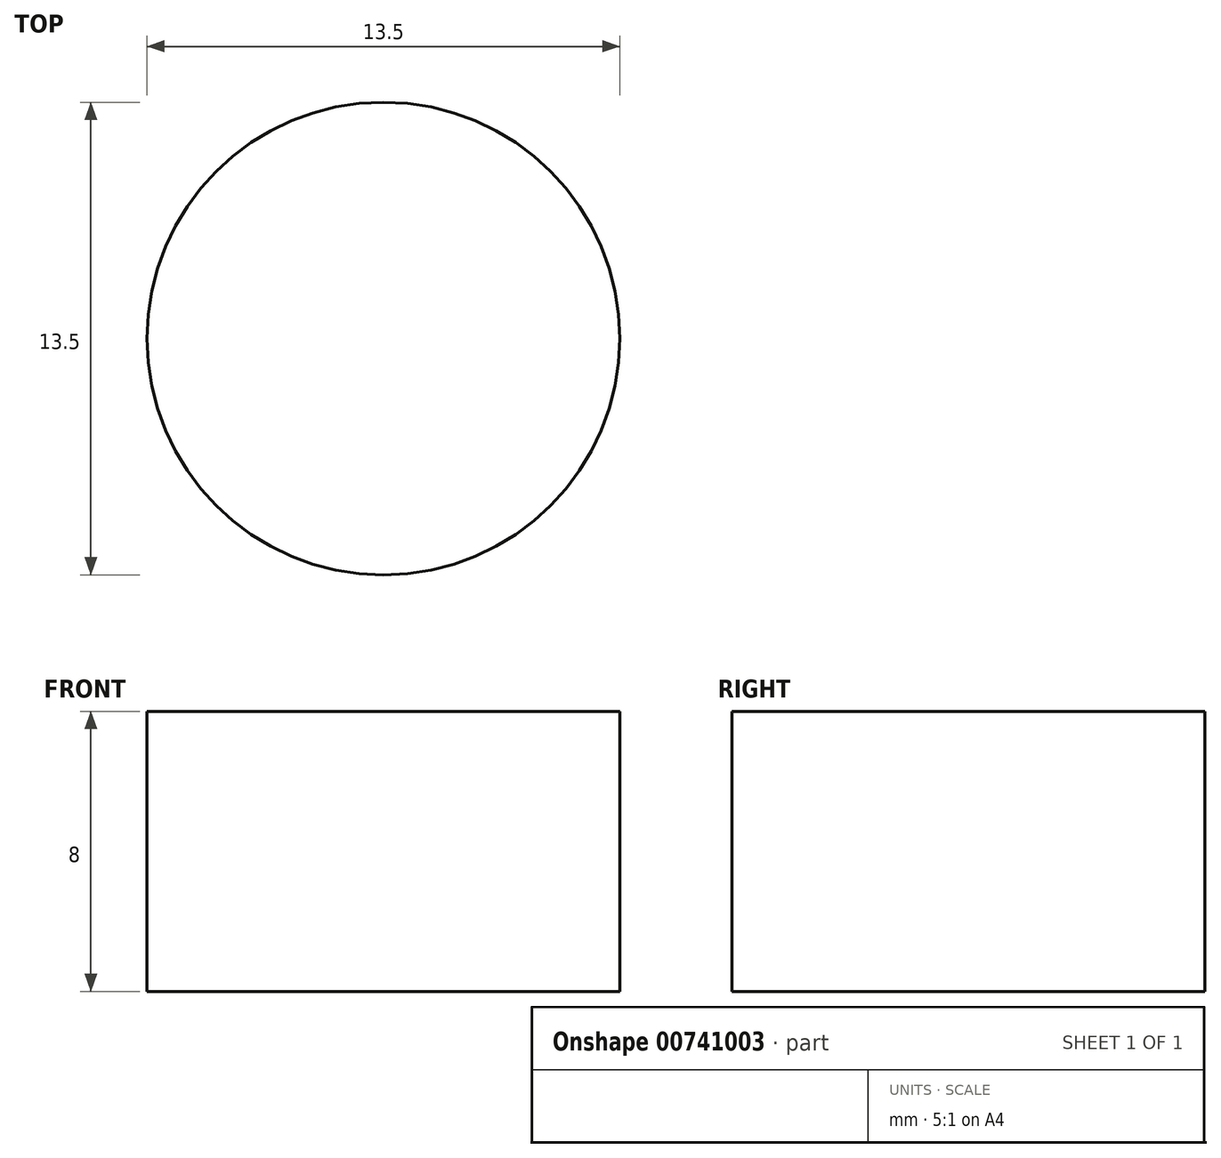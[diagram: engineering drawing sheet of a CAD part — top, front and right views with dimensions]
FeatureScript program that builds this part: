
annotation { "Feature Type Name" : "Feature", "Feature Type Description" : "" }
export const myFeature = defineFeature(function(context is Context, id is Id, definition is map)
    precondition{}
    {
        {
            var Q0;
            Q0=qCreatedBy(makeId("Top.planeOp"),FACE);
            var sketch = newSketch(context, id + "F0", { "sketchPlane" : qUnion([Q0])});
            skCircle(sketch, "E0", {"center": v(0, 0) * mm, "radius": 6.75 * mm});
            skSolve(sketch);
        }
        {
            var Q0;
            Q0=makeQuery(id+"F0.imprint","IMPRINT",FACE,{"disambiguationData":[TD([[makeQuery(id+"F0.imprint","IMPRINT",EDGE,{"derivedFrom":sQuery(id+"F0.wireOp",EDGE,"E0")}),1.0]])]});
            extrude(context, id + "F1", {"entities" : qUnion([Q0]), "depth" : 8 * mm, "offsetDistance" : 25 * mm});
        }
    });
